# Revit family: Plumbing Fixture_Water Heater_Stiebel Eltron_DEL
name_source: partatom
category: Plumbing Fixtures
revit_build: Autodesk Revit 2015 (Build: 20140606_1530(x64)
units: mm (PartAtom-declared; Revit-internal decimal feet)

## types (2) — shared parameters
CW Connection = Yes
Description = Instantaneous 3 Phase Electric Water Heater - Up to 50°Celsius
HW Connection = Yes
Manufacturer = Stiebel Eltron
Manufacturer_Overall Depth = 105 mm
Manufacturer_Overall Height = 478 mm
Manufacturer_Overall Width = 225 mm
Manufacturer_URL__Product Specific = http://www.stiebel.com.au
Type Comments = Instantaneous Water Heater
URL = http://www.stiebel.com.au
Vent Connection = No
Waste Connection = No

## per-type parameters (varying)
| type | ApparentLoad_ANZRS | Manufacturer_Spec Code | Model |
| 18 AU | 19407 VA | DEL 18 AU | DEL 18 AU |
| 27 AU | 28752 VA | DEL 27 AU | DEL 27 AU |

## geometry (parser evidence)
native form markers: Sweep x2
no freeform markers — native parametric forms only
